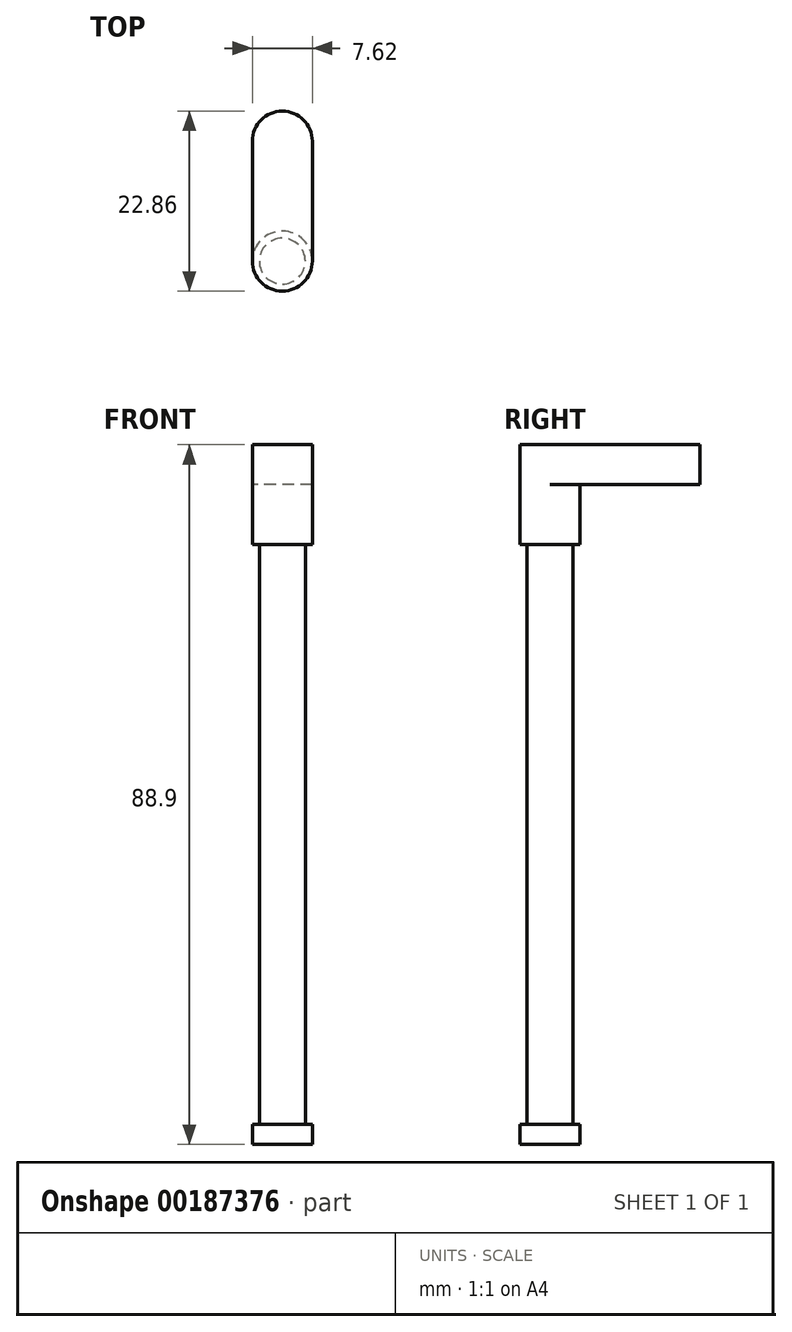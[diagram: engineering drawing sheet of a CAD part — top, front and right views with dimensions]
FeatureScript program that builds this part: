
annotation { "Feature Type Name" : "Feature", "Feature Type Description" : "" }
export const myFeature = defineFeature(function(context is Context, id is Id, definition is map)
    precondition{}
    {
        {
            var Q0;
            Q0=qCreatedBy(makeId("Top.planeOp"),FACE);
            var sketch = newSketch(context, id + "F0", { "sketchPlane" : qUnion([Q0])});
            skCircle(sketch, "E0", {"center": v(0, 0) * mm, "radius": 2.92 * mm});
            skSolve(sketch);
        }
        {
            var Q0;
            Q0=makeQuery(id+"F0.imprint","IMPRINT",FACE,{"disambiguationData":[TD([[makeQuery(id+"F0.imprint","IMPRINT",EDGE,{"derivedFrom":sQuery(id+"F0.wireOp",EDGE,"E0")}),1.0]])]});
            extrude(context, id + "F1", {"entities" : qUnion([Q0]), "depth" : 73.66 * mm});
        }
        {
            var Q0;
            Q0=makeQuery(id+"F1.opExtrude","CAP_FACE",FACE,{"disambiguationData":[OSD([sQuery(id+"F0.wireOp",EDGE,"E0")])],"isStart":true});
            var sketch = newSketch(context, id + "F2", { "sketchPlane" : qUnion([Q0])});
            skCircle(sketch, "E1", {"center": v(0, 0) * mm, "radius": 3.81 * mm});
            skSolve(sketch);
        }
        {
            var Q0;
            Q0=makeQuery(id+"F2.imprint","IMPRINT",FACE,{"disambiguationData":[TD([[makeQuery(id+"F2.imprint","IMPRINT",EDGE,{"derivedFrom":makeQuery(id+"F1.opExtrude","CAP_EDGE",EDGE,{"disambiguationData":[OSD([sQuery(id+"F0.wireOp",EDGE,"E0")])],"isStart":true})}),-1.0]])]});
            var Q1;
            Q1=makeQuery(id+"F2.imprint","IMPRINT",FACE,{"disambiguationData":[TD([[makeQuery(id+"F2.imprint","IMPRINT",EDGE,{"derivedFrom":sQuery(id+"F2.wireOp",EDGE,"E1")}),1.0]])]});
            extrude(context, id + "F3", {"entities" : qUnion([Q0, Q1]), "operationType" : NewBodyOperationType.ADD, "depth" : 2.54 * mm});
        }
        {
            var Q0;
            Q0=makeQuery(id+"F1.opExtrude","CAP_FACE",FACE,{"disambiguationData":[OSD([sQuery(id+"F0.wireOp",EDGE,"E0")])],"isStart":false});
            var sketch = newSketch(context, id + "F4", { "sketchPlane" : qUnion([Q0])});
            skCircle(sketch, "E2", {"center": v(0, 0) * mm, "radius": 3.81 * mm});
            skSolve(sketch);
        }
        {
            var Q0;
            Q0 = qSketchRegion(id + "F4", true);
            extrude(context, id + "F5", {"entities" : qUnion([Q0]), "operationType" : NewBodyOperationType.ADD, "depth" : 7.62 * mm});
        }
        {
            var Q0;
            Q0=makeQuery(id+"F5.opExtrude","CAP_FACE",FACE,{"disambiguationData":[OSD([sQuery(id+"F4.wireOp",EDGE,"E2")])],"isStart":false});
            var sketch = newSketch(context, id + "F6", { "sketchPlane" : qUnion([Q0])});
            skLineSegment(sketch, "E3.bottom", {"start": v(3.81, 0) * mm, "end": v(-3.8, 0) * mm});
            skLineSegment(sketch, "E3.top", {"start": v(3.8, 15.24) * mm, "end": v(-3.81, 15.24) * mm});
            skLineSegment(sketch, "E3.left", {"start": v(3.81, 0) * mm, "end": v(3.81, 15.24) * mm});
            skLineSegment(sketch, "E3.right", {"start": v(-3.8, 0) * mm, "end": v(-3.81, 15.24) * mm});
            skCircle(sketch, "E4", {"center": v(0, 15.24) * mm, "radius": 3.81 * mm});
            skSolve(sketch);
        }
        {
            var Q0;
            {var subQ0=sQuery(id+"F6.wireOp",EDGE,"E3.left");Q0=makeQuery(id+"F6.imprint","IMPRINT",FACE,{"disambiguationData":[TD([[makeQuery(id+"F6.imprint","IMPRINT",EDGE,{"derivedFrom":subQ0}),1.0]])]});}
            var Q1;
            {var subQ0=sQuery(id+"F6.wireOp",EDGE,"E3.bottom");Q1=makeQuery(id+"F6.imprint","IMPRINT",FACE,{"disambiguationData":[TD([[makeQuery(id+"F6.imprint","IMPRINT",EDGE,{"derivedFrom":subQ0}),-1.0]])]});}
            var Q2;
            {var subQ0=sQuery(id+"F6.wireOp",EDGE,"E3.bottom");Q2=makeQuery(id+"F6.imprint","IMPRINT",FACE,{"disambiguationData":[TD([[makeQuery(id+"F6.imprint","IMPRINT",EDGE,{"derivedFrom":subQ0}),1.0]])]});}
            var Q3;
            {var subQ0=sQuery(id+"F6.wireOp",EDGE,"E3.top");Q3=makeQuery(id+"F6.imprint","IMPRINT",FACE,{"disambiguationData":[TD([[makeQuery(id+"F6.imprint","IMPRINT",EDGE,{"derivedFrom":subQ0}),-1.0]])]});}
            var Q4;
            {var subQ0=sQuery(id+"F6.wireOp",EDGE,"E3.top");Q4=makeQuery(id+"F6.imprint","IMPRINT",FACE,{"disambiguationData":[TD([[makeQuery(id+"F6.imprint","IMPRINT",EDGE,{"derivedFrom":subQ0}),1.0]])]});}
            extrude(context, id + "F7", {"entities" : qUnion([Q0, Q1, Q2, Q3, Q4]), "operationType" : NewBodyOperationType.ADD, "depth" : 5.08 * mm});
        }
    });
